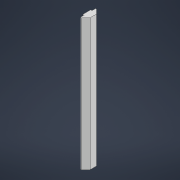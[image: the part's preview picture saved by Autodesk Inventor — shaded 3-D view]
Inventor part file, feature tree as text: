
AUTODESK INVENTOR PART (.ipt)
format: ipt  version: 2022.1 (Build 261234000, 234)  size: 150,016 bytes
history: native  units: mm
features: fillet x2, extrude x1, hole x1, sketch x1
ambient origin geometry x8: Origin, YZ Plane, XZ Plane, XY Plane, X Axis, Y Axis, Z Axis, Center Point
bodies: Volumenkörper1 (feature_tree)
feature tree (5):
  extrude  "Extrusion1"  Depth=0.4mm
  hole  "Bohrung1"  [1 undecoded]
  fillet  "Rundung1"  [1 undecoded]
  fillet  "Rundung3"  [1 undecoded]
  sketch  "Skizze2"  dims[d0=4.0mm d1=12.0mm d2=6.0mm d3=45.0deg d4=45.0deg d5=2.0mm d6=6.0mm d7=100.0mm d8=0.0mm d9=25.0mm d10=90.0deg d11=50.0mm d12=180.0deg d13=6.1mm d14=6.0mm d15=5.6mm d16=3.4mm d17=90.0deg d18=3.4mm d19=0.0mm d20=0.4mm d25=0.4mm d26=0.4mm d27=0.4mm]
note: 3 required parameter values undecoded (feature->parameter linkage not recoverable at this tier; creation-order binding heuristic only, values carry confidence <= 0.55)
